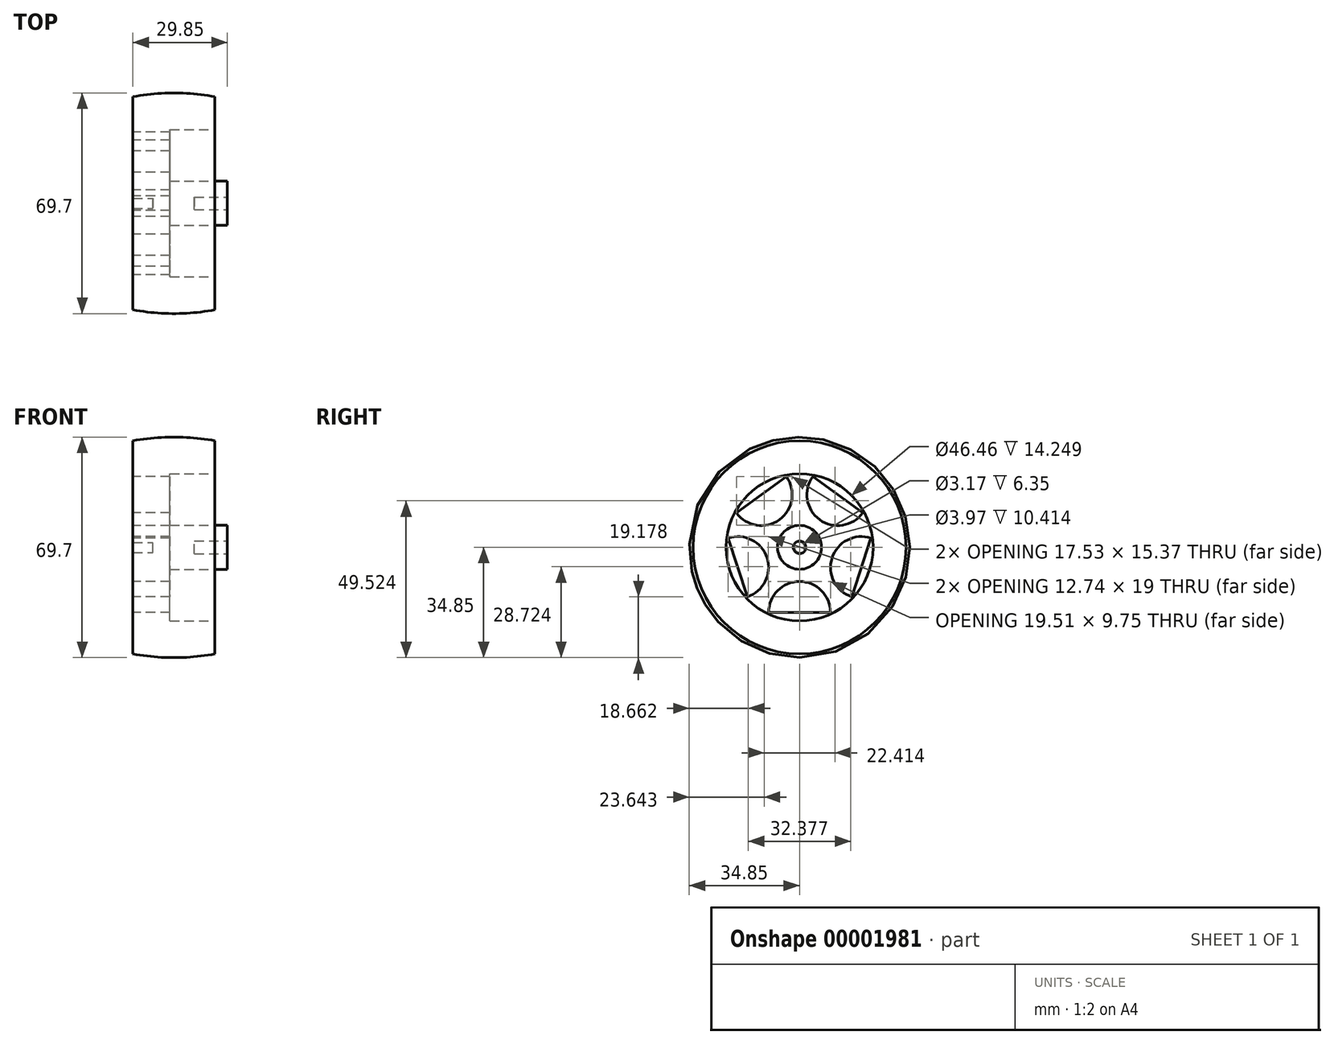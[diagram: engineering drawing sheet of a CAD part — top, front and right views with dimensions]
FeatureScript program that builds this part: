
annotation { "Feature Type Name" : "Feature", "Feature Type Description" : "" }
export const myFeature = defineFeature(function(context is Context, id is Id, definition is map)
    precondition{}
    {
        {
            var Q0;
            Q0=qCreatedBy(makeId("Front.planeOp"),FACE);
            var sketch = newSketch(context, id + "F0", { "sketchPlane" : qUnion([Q0])});
            skLineSegment(sketch, "E0", {"start": v(0, 1.98) * mm, "end": v(0, 6.95) * mm});
            skLineSegment(sketch, "E1", {"start": v(0, 6.95) * mm, "end": v(-18.19, 6.95) * mm});
            skLineSegment(sketch, "E2", {"start": v(-18.19, 6.95) * mm, "end": v(-18.19, 23.23) * mm});
            skLineSegment(sketch, "E3", {"start": v(-18.19, 23.23) * mm, "end": v(-3.94, 23.23) * mm});
            skLineSegment(sketch, "E4", {"start": v(-23.5, 0) * mm, "end": v(-10.41, 0) * mm});
            skPoint(sketch, "E5", {"position": v(-29.84, 33.66) * mm});
            skArc(sketch, "E6", {"start": v(-3.94, 33.66) * mm, "mid": v(-16.9, 34.85) * mm, "end": v(-29.84, 33.66) * mm});
            skPoint(sketch, "E7", {"position": v(-16.9, 34.85) * mm});
            skLineSegment(sketch, "E8", {"start": v(-3.94, 33.66) * mm, "end": v(-3.94, 23.23) * mm});
            skLineSegment(sketch, "E9", {"start": v(-29.84, 33.66) * mm, "end": v(-29.84, 1.59) * mm});
            skLineSegment(sketch, "E10", {"start": v(-29.84, 1.59) * mm, "end": v(-23.5, 1.59) * mm});
            skLineSegment(sketch, "E11", {"start": v(-23.5, 1.59) * mm, "end": v(-23.5, 0) * mm});
            skLineSegment(sketch, "E12", {"start": v(0, 1.98) * mm, "end": v(-10.41, 1.98) * mm});
            skLineSegment(sketch, "E13", {"start": v(-10.41, 1.98) * mm, "end": v(-10.41, 0) * mm});
            skSolve(sketch);
        }
        {
            var Q0;
            Q0=qCreatedBy(makeId("Front.planeOp"),FACE);
            var sketch = newSketch(context, id + "F1", { "sketchPlane" : qUnion([Q0])});
            skLineSegment(sketch, "E14", {"start": v(0, 0) * mm, "end": v(38.63, 0) * mm, "construction": true});
            skLineSegment(sketch, "E15", {"start": v(0, 0) * mm, "end": v(-45.14, 0) * mm, "construction": true});
            skSolve(sketch);
        }
        {
            var Q0;
            Q0=makeQuery(id+"F0.imprint","IMPRINT",FACE,{"disambiguationData":[TD([[makeQuery(id+"F0.imprint","IMPRINT",EDGE,{"derivedFrom":sQuery(id+"F0.wireOp",EDGE,"E0")}),1.0]])]});
            var Q1;
            Q1=sQuery(id+"F1.wireOp",EDGE,"E15");
            revolve(context, id + "F2", {"entities" : qUnion([Q0]), "axis" : qUnion([Q1]), "revolveType" : RevolveType.FULL});
        }
        {
            var Q0;
            Q0=makeQuery(id+"F2.opRevolve","SWEPT_FACE",FACE,{"disambiguationData":[OSD([sQuery(id+"F0.wireOp",EDGE,"E9")])]});
            var sketch = newSketch(context, id + "F3", { "sketchPlane" : qUnion([Q0])});
            skCircle(sketch, "E16.cCircle", {"center": v(0, 0) * mm, "radius": 25.4 * mm, "construction": true});
            skLineSegment(sketch, "E16.0", {"start": v(-24.16, 7.85) * mm, "end": v(-19.97, 10.9) * mm, "construction": true});
            skLineSegment(sketch, "E16.1", {"start": v(0, 25.4) * mm, "end": v(4.19, 22.36) * mm, "construction": true});
            skLineSegment(sketch, "E16.2", {"start": v(24.16, 7.85) * mm, "end": v(22.56, 2.93) * mm, "construction": true});
            skLineSegment(sketch, "E16.3", {"start": v(14.93, -20.55) * mm, "end": v(9.75, -20.55) * mm, "construction": true});
            skLineSegment(sketch, "E16.4", {"start": v(-14.93, -20.55) * mm, "end": v(-16.53, -15.63) * mm, "construction": true});
            skCircle(sketch, "E17", {"center": v(0, 0) * mm, "radius": 10.8 * mm, "construction": true});
            skArc(sketch, "E18", {"start": v(-19.97, 10.9) * mm, "mid": v(-6.35, 8.73) * mm, "end": v(-4.19, 22.36) * mm});
            skArc(sketch, "E19", {"start": v(4.19, 22.36) * mm, "mid": v(6.35, 8.73) * mm, "end": v(19.97, 10.9) * mm});
            skArc(sketch, "E20", {"start": v(22.56, 2.93) * mm, "mid": v(10.27, -3.34) * mm, "end": v(16.53, -15.63) * mm});
            skArc(sketch, "E21", {"start": v(9.75, -20.55) * mm, "mid": v(0, -10.8) * mm, "end": v(-9.75, -20.55) * mm});
            skArc(sketch, "E22", {"start": v(-16.53, -15.63) * mm, "mid": v(-10.27, -3.34) * mm, "end": v(-22.56, 2.93) * mm});
            skLineSegment(sketch, "E23", {"start": v(4.19, 22.36) * mm, "end": v(19.97, 10.9) * mm});
            skLineSegment(sketch, "E24", {"start": v(19.97, 10.9) * mm, "end": v(24.16, 7.85) * mm, "construction": true});
            skLineSegment(sketch, "E25", {"start": v(22.56, 2.93) * mm, "end": v(16.53, -15.63) * mm});
            skLineSegment(sketch, "E26", {"start": v(16.53, -15.63) * mm, "end": v(14.93, -20.55) * mm, "construction": true});
            skLineSegment(sketch, "E27", {"start": v(9.75, -20.55) * mm, "end": v(-9.75, -20.55) * mm});
            skLineSegment(sketch, "E28", {"start": v(-9.75, -20.55) * mm, "end": v(-14.93, -20.55) * mm, "construction": true});
            skLineSegment(sketch, "E29", {"start": v(-16.53, -15.63) * mm, "end": v(-22.56, 2.93) * mm});
            skLineSegment(sketch, "E30", {"start": v(-22.56, 2.93) * mm, "end": v(-24.16, 7.85) * mm, "construction": true});
            skLineSegment(sketch, "E31", {"start": v(-19.97, 10.9) * mm, "end": v(-4.19, 22.36) * mm});
            skArc(sketch, "E32", {"start": v(-4.19, 22.36) * mm, "mid": v(-19.97, 10.9) * mm, "end": v(-4.19, 22.36) * mm, "construction": true});
            skLineSegment(sketch, "E33", {"start": v(-4.19, 22.36) * mm, "end": v(0, 25.4) * mm, "construction": true});
            skSolve(sketch);
        }
        {
            var Q0;
            Q0=makeQuery(id+"F3.imprint","IMPRINT",FACE,{"disambiguationData":[TD([[makeQuery(id+"F3.imprint","IMPRINT",EDGE,{"derivedFrom":sQuery(id+"F3.wireOp",EDGE,"E18")}),1.0]])]});
            var Q1;
            Q1=makeQuery(id+"F3.imprint","IMPRINT",FACE,{"disambiguationData":[TD([[makeQuery(id+"F3.imprint","IMPRINT",EDGE,{"derivedFrom":sQuery(id+"F3.wireOp",EDGE,"E19")}),1.0]])]});
            var Q2;
            Q2=makeQuery(id+"F3.imprint","IMPRINT",FACE,{"disambiguationData":[TD([[makeQuery(id+"F3.imprint","IMPRINT",EDGE,{"derivedFrom":sQuery(id+"F3.wireOp",EDGE,"E20")}),1.0]])]});
            var Q3;
            Q3=makeQuery(id+"F3.imprint","IMPRINT",FACE,{"disambiguationData":[TD([[makeQuery(id+"F3.imprint","IMPRINT",EDGE,{"derivedFrom":sQuery(id+"F3.wireOp",EDGE,"E21")}),1.0]])]});
            var Q4;
            Q4=makeQuery(id+"F3.imprint","IMPRINT",FACE,{"disambiguationData":[TD([[makeQuery(id+"F3.imprint","IMPRINT",EDGE,{"derivedFrom":sQuery(id+"F3.wireOp",EDGE,"E22")}),1.0]])]});
            extrude(context, id + "F4", {"entities" : qUnion([Q0, Q1, Q2, Q3, Q4]), "operationType" : NewBodyOperationType.REMOVE, "endBound" : BoundingType.UP_TO_NEXT, "oppositeDirection" : true, "depth" : 25.4 * mm});
        }
    });
